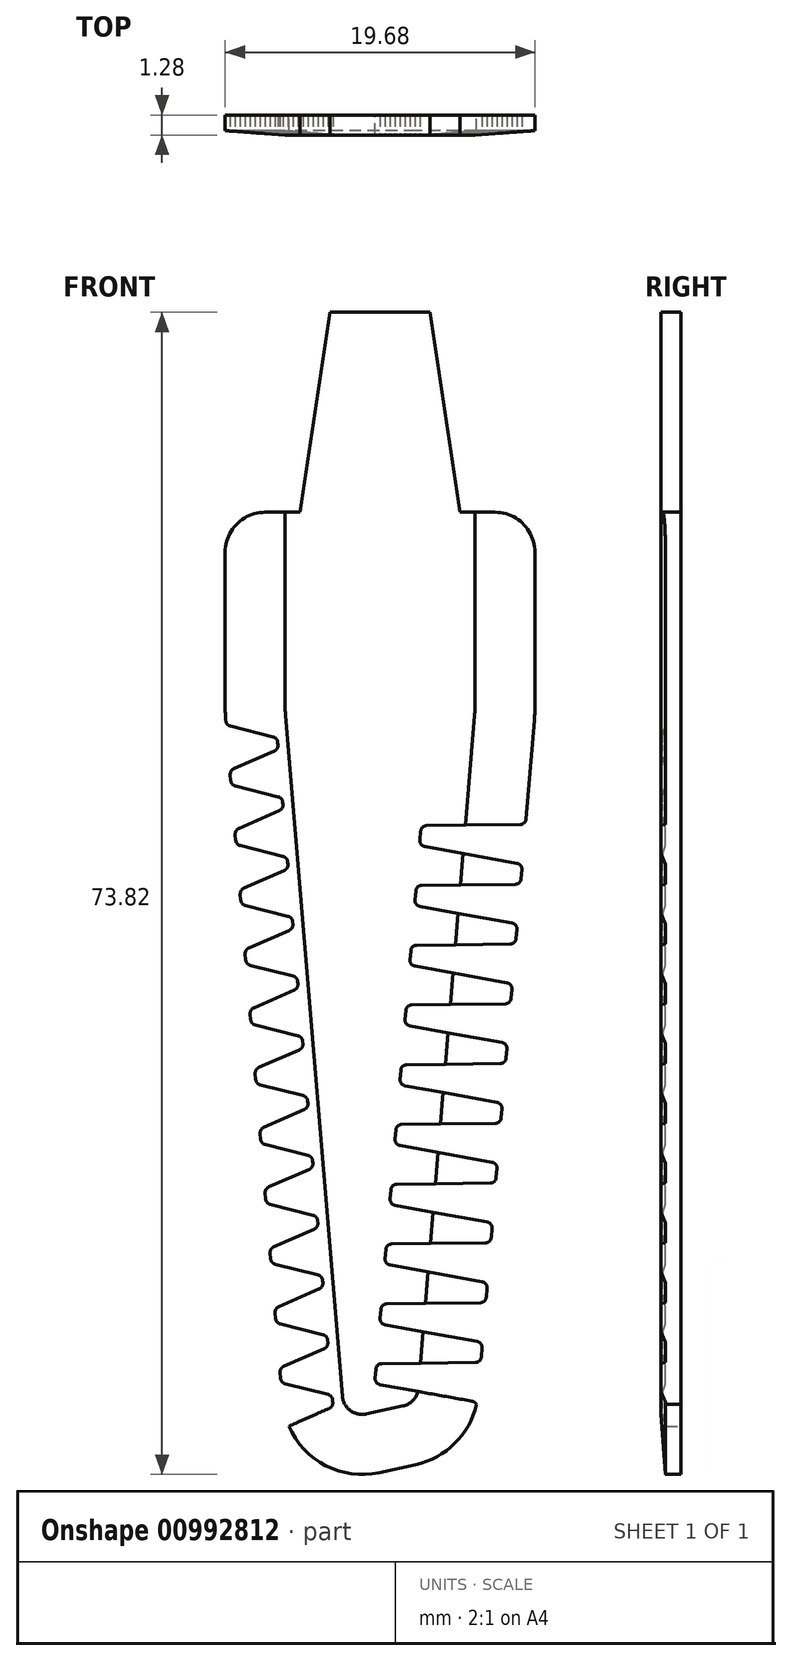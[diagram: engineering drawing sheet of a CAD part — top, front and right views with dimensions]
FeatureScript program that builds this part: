
annotation { "Feature Type Name" : "Feature", "Feature Type Description" : "" }
export const myFeature = defineFeature(function(context is Context, id is Id, definition is map)
    precondition{}
    {
        {
            var Q0;
            Q0=qCreatedBy(makeId("Front.planeOp"),FACE);
            var sketch = newSketch(context, id + "F0", { "sketchPlane" : qUnion([Q0])});
            skLineSegment(sketch, "E0", {"start": v(-5.71, -62.23) * mm, "end": v(0, -62.23) * mm});
            skLineSegment(sketch, "E1", {"start": v(0, -62.23) * mm, "end": v(5.72, -62.23) * mm});
            skLineSegment(sketch, "E2", {"start": v(5.72, -62.23) * mm, "end": v(9.84, -12.7) * mm});
            skLineSegment(sketch, "E3", {"start": v(9.84, 0) * mm, "end": v(0, 0) * mm});
            skLineSegment(sketch, "E4", {"start": v(-3.18, 0) * mm, "end": v(-3.18, 12.7) * mm});
            skLineSegment(sketch, "E5", {"start": v(-3.18, 12.7) * mm, "end": v(0, 12.7) * mm});
            skLineSegment(sketch, "E6", {"start": v(0, 12.7) * mm, "end": v(3.18, 12.7) * mm});
            skLineSegment(sketch, "E7", {"start": v(3.18, 12.7) * mm, "end": v(3.18, 0) * mm});
            skLineSegment(sketch, "E8", {"start": v(9.84, -12.7) * mm, "end": v(9.84, 0) * mm});
            skLineSegment(sketch, "E9", {"start": v(0, 0) * mm, "end": v(-9.84, 0) * mm});
            skLineSegment(sketch, "E10", {"start": v(-9.84, 0) * mm, "end": v(-9.84, -12.7) * mm});
            skLineSegment(sketch, "E11", {"start": v(-9.84, -12.7) * mm, "end": v(-5.71, -62.23) * mm});
            skLineSegment(sketch, "E12", {"start": v(-9.84, -12.7) * mm, "end": v(9.84, -12.7) * mm, "construction": true});
            skLineSegment(sketch, "E13", {"start": v(-5.72, -62.23) * mm, "end": v(5.93, -59.7) * mm});
            skSolve(sketch);
        }
        {
            var Q0;
            {var subQ0=sQuery(id+"F0.wireOp",EDGE,"E8");Q0=makeQuery(id+"F0.imprint","IMPRINT",FACE,{"disambiguationData":[TD([[makeQuery(id+"F0.imprint","IMPRINT",EDGE,{"derivedFrom":subQ0}),1.0]])]});}
            extrude(context, id + "F1", {"entities" : qUnion([Q0]), "endBound" : BoundingType.SYMMETRIC, "depth" : 1.27 * mm, "offsetDistance" : 25.4 * mm});
        }
        {
            var Q0;
            Q0=makeQuery(id+"F1.opExtrude","SWEPT_EDGE",EDGE,{"disambiguationData":[OSD([sQuery(id+"F0.wireOp",EDGE,"E10"),sQuery(id+"F0.wireOp",EDGE,"E11")])]});
            var Q1;
            Q1=makeQuery(id+"F1.opExtrude","SWEPT_EDGE",EDGE,{"disambiguationData":[OSD([sQuery(id+"F0.wireOp",EDGE,"E2"),sQuery(id+"F0.wireOp",EDGE,"E8")])]});
            fillet(context, id + "F2", {"entities" : qUnion([Q0, Q1]), "radius" : 12.7 * mm, "tangentPropagation" : true, "defaultsChanged" : false, "vertexSettings" : [], "allowEdgeOverflow" : false});
        }
        {
            var Q0;
            Q0=makeQuery(id+"F1.opExtrude","SWEPT_EDGE",EDGE,{"disambiguationData":[OSD([sQuery(id+"F0.wireOp",EDGE,"E3"),sQuery(id+"F0.wireOp",EDGE,"E8")])]});
            var Q1;
            Q1=makeQuery(id+"F1.opExtrude","SWEPT_EDGE",EDGE,{"disambiguationData":[OSD([sQuery(id+"F0.wireOp",EDGE,"E9"),sQuery(id+"F0.wireOp",EDGE,"E10")])]});
            fillet(context, id + "F3", {"entities" : qUnion([Q0, Q1]), "radius" : 2.54 * mm, "tangentPropagation" : true, "allowEdgeOverflow" : false});
        }
        {
            var Q0;
            Q0=makeQuery(id+"F11.boolean.opBoolean","MERGE",EDGE,{"derivedFrom":[makeQuery(id+"F1.opExtrude","SWEPT_EDGE",EDGE,{"disambiguationData":[OSD([sQuery(id+"F0.wireOp",EDGE,"qJLN5KsG-3gIc-xckK-YI7e-Zwq7uVVBdTZE"),sQuery(id+"F0.wireOp",EDGE,"E0")])]})],"fromTools":[makeQuery(id+"F11.opExtrude","SWEPT_EDGE",EDGE,{"disambiguationData":[OSD([sQuery(id+"F10.wireOp",EDGE,"E32"),sQuery(id+"F10.wireOp",EDGE,"E34")])]})]});
            fillet(context, id + "F4", {"entities" : qUnion([Q0]), "radius" : 5.08 * mm, "tangentPropagation" : true, "defaultsChanged" : true, "vertexSettings" : [], "allowEdgeOverflow" : false});
        }
        {
            var Q0;
            Q0=makeQuery(id+"F11.boolean.opBoolean","COPY",EDGE,{"derivedFrom":makeQuery(id+"F11.opExtrude","SWEPT_EDGE",EDGE,{"disambiguationData":[OSD([sQuery(id+"F10.wireOp",EDGE,"E32"),sQuery(id+"F10.wireOp",EDGE,"E33")])]})});
            var Q1;
            Q1=makeQuery(id+"F1.opExtrude","SWEPT_EDGE",EDGE,{"disambiguationData":[OSD([sQuery(id+"F0.wireOp",EDGE,"E1"),sQuery(id+"F0.wireOp",EDGE,"E2")])]});
            fillet(context, id + "F5", {"entities" : qUnion([Q0, Q1]), "radius" : 5.08 * mm, "tangentPropagation" : true, "defaultsChanged" : true, "vertexSettings" : [], "allowEdgeOverflow" : false});
        }
        {
            var Q0;
            Q0=qCreatedBy(makeId("Top.planeOp"),FACE);
            var sketch = newSketch(context, id + "F6", { "sketchPlane" : qUnion([Q0])});
            skLineSegment(sketch, "E14", {"start": v(6.03, 0.63) * mm, "end": v(9.84, 0.64) * mm});
            skLineSegment(sketch, "E15", {"start": v(9.84, 0.64) * mm, "end": v(9.84, 0.35) * mm});
            skLineSegment(sketch, "E16", {"start": v(9.84, 0.35) * mm, "end": v(9.84, 0) * mm, "construction": true});
            skLineSegment(sketch, "E17", {"start": v(9.84, 0) * mm, "end": v(9.84, -0.35) * mm, "construction": true});
            skLineSegment(sketch, "E18", {"start": v(9.84, -0.35) * mm, "end": v(9.84, -0.64) * mm});
            skLineSegment(sketch, "E19", {"start": v(9.84, -0.64) * mm, "end": v(6.03, -0.64) * mm});
            skLineSegment(sketch, "E20", {"start": v(6.03, -0.64) * mm, "end": v(9.84, -0.35) * mm});
            skLineSegment(sketch, "E21", {"start": v(6.03, 0.63) * mm, "end": v(9.84, 0.35) * mm});
            skLineSegment(sketch, "E22", {"start": v(6.03, 0.63) * mm, "end": v(6.03, -0.64) * mm, "construction": true});
            skSolve(sketch);
        }
        {
            var Q0;
            Q0=qCreatedBy(makeId("Front.planeOp"),FACE);
            var sketch = newSketch(context, id + "F7", { "sketchPlane" : qUnion([Q0])});
            skArc(sketch, "E23.0", {"start": v(6.24, -55.95) * mm, "mid": v(5, -58.88) * mm, "end": v(2.25, -60.5) * mm});
            skArc(sketch, "E24.0", {"start": v(-0.05, -61) * mm, "mid": v(-4.15, -60.12) * mm, "end": v(-6.2, -56.46) * mm});
            skLineSegment(sketch, "E25", {"start": v(2.25, -60.5) * mm, "end": v(-0.05, -61) * mm});
            skLineSegment(sketch, "E26", {"start": v(-6.2, -56.46) * mm, "end": v(-9.8, -13.23) * mm});
            skArc(sketch, "E27.0", {"start": v(9.84, -12.17) * mm, "mid": v(9.83, -12.7) * mm, "end": v(9.8, -13.23) * mm});
            skLineSegment(sketch, "E28", {"start": v(9.84, -12.17) * mm, "end": v(9.84, 0) * mm});
            skLineSegment(sketch, "E29", {"start": v(9.8, -13.23) * mm, "end": v(6.24, -55.95) * mm});
            skArc(sketch, "E30.0", {"start": v(-9.8, -13.23) * mm, "mid": v(-9.83, -12.7) * mm, "end": v(-9.84, -12.17) * mm});
            skLineSegment(sketch, "E31", {"start": v(-9.84, -12.17) * mm, "end": v(-9.84, 1.67) * mm});
            skSolve(sketch);
        }
        {
            var Q0;
            Q0=makeQuery(id+"F6.imprint","IMPRINT",FACE,{"disambiguationData":[TD([[makeQuery(id+"F6.imprint","IMPRINT",EDGE,{"derivedFrom":sQuery(id+"F6.wireOp",EDGE,"E18")}),-1.0]])]});
            var Q1;
            Q1 = qConstructionFilter(qBodyType(qCreatedBy(id + "F6" ,EDGE), BodyType.WIRE), ConstructionObject.NO);
            var Q2;
            Q2 = qConstructionFilter(qBodyType(qCreatedBy(id + "F7" ,EDGE), BodyType.WIRE), ConstructionObject.NO);
            sweep(context, id + "F8", {"profiles" : qUnion([Q0]), "surfaceProfiles" : qUnion([Q1]), "path" : qUnion([Q2])});
        }
        {
            var Q0;
            Q0=makeQuery(id+"F8.opSweep","SWEPT_BODY",BODY,{"disambiguationData":[OSD([sQuery(id+"F6.wireOp",EDGE,"E14"),sQuery(id+"F6.wireOp",EDGE,"E15"),sQuery(id+"F6.wireOp",EDGE,"E21"),sQuery(id+"F7.wireOp",EDGE,"E28")])]});
            var Q1;
            Q1=makeQuery(id+"F8.opSweep","SWEPT_BODY",BODY,{"disambiguationData":[OSD([sQuery(id+"F6.wireOp",EDGE,"E18"),sQuery(id+"F6.wireOp",EDGE,"E19"),sQuery(id+"F6.wireOp",EDGE,"E20"),sQuery(id+"F7.wireOp",EDGE,"E28")])]});
            var Q2;
            Q2=makeQuery(id+"F1.opExtrude","SWEPT_BODY",BODY,{"disambiguationData":[OSD([sQuery(id+"F0.wireOp",EDGE,"E0"),sQuery(id+"F0.wireOp",EDGE,"E1"),sQuery(id+"F0.wireOp",EDGE,"E2"),sQuery(id+"F0.wireOp",EDGE,"E3"),sQuery(id+"F0.wireOp",EDGE,"E4"),sQuery(id+"F0.wireOp",EDGE,"E5"),sQuery(id+"F0.wireOp",EDGE,"E6"),sQuery(id+"F0.wireOp",EDGE,"E7"),sQuery(id+"F0.wireOp",EDGE,"E8"),sQuery(id+"F0.wireOp",EDGE,"E9"),sQuery(id+"F0.wireOp",EDGE,"E10"),sQuery(id+"F0.wireOp",EDGE,"E11")])]});
            booleanBodies(context, id + "F9", {"operationType" : BooleanOperationType.SUBTRACTION, "tools" : qUnion([Q0, Q1]), "targets" : qUnion([Q2])});
        }
        {
            var Q0;
            Q0=qCreatedBy(makeId("Front.planeOp"),FACE);
            var sketch = newSketch(context, id + "F10", { "sketchPlane" : qUnion([Q0])});
            skLineSegment(sketch, "E32", {"start": v(-5.71, -62.23) * mm, "end": v(5.82, -60.96) * mm});
            skLineSegment(sketch, "E33", {"start": v(5.82, -60.96) * mm, "end": v(5.72, -62.23) * mm});
            skLineSegment(sketch, "E34", {"start": v(5.72, -62.23) * mm, "end": v(-5.71, -62.23) * mm});
            skSolve(sketch);
        }
        {
            var Q0;
            Q0=qSketchRegion(id+"F10",true);
            extrude(context, id + "F11", {"entities" : qUnion([Q0]), "operationType" : NewBodyOperationType.REMOVE, "endBound" : BoundingType.SYMMETRIC, "depth" : 25.4 * mm, "offsetDistance" : 25.4 * mm});
        }
        {
            var Q0;
            Q0=qCreatedBy(makeId("Front.planeOp"),FACE);
            var sketch = newSketch(context, id + "F12", { "sketchPlane" : qUnion([Q0])});
            skArc(sketch, "E35", {"start": v(6.16, -56.88) * mm, "mid": v(6.08, -56.61) * mm, "end": v(5.85, -56.47) * mm});
            skArc(sketch, "E36", {"start": v(6.05, -54) * mm, "mid": v(6.3, -53.9) * mm, "end": v(6.43, -53.65) * mm});
            skLineSegment(sketch, "E37", {"start": v(0.11, -54.08) * mm, "end": v(0, -55.41) * mm, "construction": true});
            skLineSegment(sketch, "E38", {"start": v(6.43, -53.65) * mm, "end": v(6.16, -56.88) * mm});
            skArc(sketch, "E39", {"start": v(0.11, -54.08) * mm, "mid": v(-0.14, -54.18) * mm, "end": v(-0.26, -54.43) * mm});
            skArc(sketch, "E40", {"start": v(-0.31, -55) * mm, "mid": v(-0.23, -55.27) * mm, "end": v(0, -55.41) * mm});
            skLineSegment(sketch, "E41", {"start": v(5.85, -56.47) * mm, "end": v(6.19, -56.53) * mm, "construction": true});
            skLineSegment(sketch, "E42", {"start": v(6.05, -54) * mm, "end": v(6.4, -54) * mm, "construction": true});
            skLineSegment(sketch, "E43", {"start": v(0, -55.41) * mm, "end": v(5.85, -56.47) * mm});
            skLineSegment(sketch, "E44", {"start": v(6.05, -54) * mm, "end": v(0.11, -54.08) * mm});
            skLineSegment(sketch, "E45", {"start": v(-0.31, -55) * mm, "end": v(-0.34, -55.35) * mm, "construction": true});
            skLineSegment(sketch, "E46", {"start": v(-0.34, -55.35) * mm, "end": v(0, -55.41) * mm, "construction": true});
            skLineSegment(sketch, "E47", {"start": v(-0.26, -54.43) * mm, "end": v(-0.24, -54.08) * mm, "construction": true});
            skLineSegment(sketch, "E48", {"start": v(-0.24, -54.08) * mm, "end": v(0.11, -54.08) * mm, "construction": true});
            skLineSegment(sketch, "E49", {"start": v(-0.29, -54.72) * mm, "end": v(6.3, -55.26) * mm, "construction": true});
            skLineSegment(sketch, "E50", {"start": v(-0.26, -54.43) * mm, "end": v(-0.29, -54.72) * mm});
            skLineSegment(sketch, "E51", {"start": v(-0.29, -54.72) * mm, "end": v(-0.31, -55) * mm});
            skSolve(sketch);
        }
        {
            var Q0;
            Q0=qSketchRegion(id+"F12",true);
            extrude(context, id + "F13", {"entities" : qUnion([Q0]), "operationType" : NewBodyOperationType.REMOVE, "endBound" : BoundingType.SYMMETRIC, "depth" : 25.4 * mm, "offsetDistance" : 25.4 * mm});
        }
        {
            var Q0;
            Q0=qCreatedBy(makeId("Front.planeOp"),FACE);
            var sketch = newSketch(context, id + "F14", { "sketchPlane" : qUnion([Q0])});
            skArc(sketch, "E52.0", {"start": v(6.05, -54) * mm, "mid": v(6.3, -53.9) * mm, "end": v(6.43, -53.65) * mm});
            skLineSegment(sketch, "E53.0", {"start": v(6.05, -54) * mm, "end": v(0.11, -54.08) * mm});
            skLineSegment(sketch, "E54.0", {"start": v(6.43, -53.65) * mm, "end": v(6.16, -56.88) * mm});
            skArc(sketch, "E55.0", {"start": v(6.16, -56.88) * mm, "mid": v(6.08, -56.61) * mm, "end": v(5.85, -56.47) * mm});
            skLineSegment(sketch, "E56.0", {"start": v(0, -55.41) * mm, "end": v(5.85, -56.47) * mm});
            skArc(sketch, "E57.0", {"start": v(0.11, -54.08) * mm, "mid": v(-0.14, -54.18) * mm, "end": v(-0.26, -54.43) * mm});
            skArc(sketch, "E58.0", {"start": v(-0.31, -55) * mm, "mid": v(-0.23, -55.27) * mm, "end": v(0, -55.41) * mm});
            skLineSegment(sketch, "E59.0", {"start": v(-0.26, -54.43) * mm, "end": v(-0.29, -54.72) * mm});
            skLineSegment(sketch, "E60.0", {"start": v(-0.29, -54.72) * mm, "end": v(-0.31, -55) * mm});
            skLineSegment(sketch, "E61.1.0.0", {"start": v(6.75, -49.86) * mm, "end": v(6.48, -53.08) * mm});
            skLineSegment(sketch, "E61.1.0.1", {"start": v(6.37, -50.2) * mm, "end": v(0.43, -50.28) * mm});
            skLineSegment(sketch, "E61.1.0.2", {"start": v(0.32, -51.61) * mm, "end": v(6.17, -52.67) * mm});
            skArc(sketch, "E61.1.0.3", {"start": v(6.37, -50.2) * mm, "mid": v(6.63, -50.1) * mm, "end": v(6.75, -49.86) * mm});
            skArc(sketch, "E61.1.0.4", {"start": v(6.48, -53.08) * mm, "mid": v(6.4, -52.81) * mm, "end": v(6.17, -52.67) * mm});
            skLineSegment(sketch, "E61.1.0.5", {"start": v(0.03, -50.92) * mm, "end": v(0, -51.2) * mm});
            skArc(sketch, "E61.1.0.6", {"start": v(0, -51.2) * mm, "mid": v(0.08, -51.47) * mm, "end": v(0.32, -51.61) * mm});
            skArc(sketch, "E61.1.0.7", {"start": v(0.43, -50.28) * mm, "mid": v(0.17, -50.38) * mm, "end": v(0.05, -50.63) * mm});
            skLineSegment(sketch, "E61.1.0.8", {"start": v(0.05, -50.63) * mm, "end": v(0.03, -50.92) * mm});
            skLineSegment(sketch, "E61.2.0.0", {"start": v(7.06, -46.06) * mm, "end": v(6.8, -49.28) * mm});
            skLineSegment(sketch, "E61.2.0.1", {"start": v(6.69, -46.4) * mm, "end": v(0.74, -46.49) * mm});
            skLineSegment(sketch, "E61.2.0.2", {"start": v(0.63, -47.82) * mm, "end": v(6.48, -48.88) * mm});
            skArc(sketch, "E61.2.0.3", {"start": v(6.69, -46.4) * mm, "mid": v(6.94, -46.3) * mm, "end": v(7.06, -46.06) * mm});
            skArc(sketch, "E61.2.0.4", {"start": v(6.8, -49.28) * mm, "mid": v(6.72, -49.02) * mm, "end": v(6.48, -48.88) * mm});
            skLineSegment(sketch, "E61.2.0.5", {"start": v(0.34, -47.12) * mm, "end": v(0.32, -47.41) * mm});
            skArc(sketch, "E61.2.0.6", {"start": v(0.32, -47.41) * mm, "mid": v(0.4, -47.67) * mm, "end": v(0.63, -47.82) * mm});
            skArc(sketch, "E61.2.0.7", {"start": v(0.74, -46.49) * mm, "mid": v(0.49, -46.59) * mm, "end": v(0.37, -46.83) * mm});
            skLineSegment(sketch, "E61.2.0.8", {"start": v(0.37, -46.83) * mm, "end": v(0.34, -47.12) * mm});
            skLineSegment(sketch, "E61.3.0.0", {"start": v(7.38, -42.26) * mm, "end": v(7.11, -45.48) * mm});
            skLineSegment(sketch, "E61.3.0.1", {"start": v(7, -42.61) * mm, "end": v(1.06, -42.69) * mm});
            skLineSegment(sketch, "E61.3.0.2", {"start": v(0.95, -44.02) * mm, "end": v(6.8, -45.08) * mm});
            skArc(sketch, "E61.3.0.3", {"start": v(7, -42.61) * mm, "mid": v(7.26, -42.51) * mm, "end": v(7.38, -42.26) * mm});
            skArc(sketch, "E61.3.0.4", {"start": v(7.11, -45.48) * mm, "mid": v(7.03, -45.22) * mm, "end": v(6.8, -45.08) * mm});
            skLineSegment(sketch, "E61.3.0.5", {"start": v(0.66, -43.33) * mm, "end": v(0.64, -43.61) * mm});
            skArc(sketch, "E61.3.0.6", {"start": v(0.64, -43.61) * mm, "mid": v(0.71, -43.88) * mm, "end": v(0.95, -44.02) * mm});
            skArc(sketch, "E61.3.0.7", {"start": v(1.06, -42.69) * mm, "mid": v(0.8, -42.8) * mm, "end": v(0.69, -43.04) * mm});
            skLineSegment(sketch, "E61.3.0.8", {"start": v(0.69, -43.04) * mm, "end": v(0.66, -43.33) * mm});
            skLineSegment(sketch, "E61.4.0.0", {"start": v(7.7, -38.47) * mm, "end": v(7.43, -41.69) * mm});
            skLineSegment(sketch, "E61.4.0.1", {"start": v(7.32, -38.82) * mm, "end": v(1.38, -38.9) * mm});
            skLineSegment(sketch, "E61.4.0.2", {"start": v(1.27, -40.22) * mm, "end": v(7.11, -41.28) * mm});
            skArc(sketch, "E61.4.0.3", {"start": v(7.32, -38.82) * mm, "mid": v(7.58, -38.71) * mm, "end": v(7.7, -38.47) * mm});
            skArc(sketch, "E61.4.0.4", {"start": v(7.43, -41.69) * mm, "mid": v(7.35, -41.42) * mm, "end": v(7.11, -41.28) * mm});
            skLineSegment(sketch, "E61.4.0.5", {"start": v(0.98, -39.53) * mm, "end": v(0.95, -39.82) * mm});
            skArc(sketch, "E61.4.0.6", {"start": v(0.95, -39.82) * mm, "mid": v(1.03, -40.08) * mm, "end": v(1.27, -40.22) * mm});
            skArc(sketch, "E61.4.0.7", {"start": v(1.38, -38.9) * mm, "mid": v(1.12, -39) * mm, "end": v(1, -39.24) * mm});
            skLineSegment(sketch, "E61.4.0.8", {"start": v(1, -39.24) * mm, "end": v(0.98, -39.53) * mm});
            skLineSegment(sketch, "E61.5.0.0", {"start": v(8.01, -34.67) * mm, "end": v(7.74, -37.9) * mm});
            skLineSegment(sketch, "E61.5.0.1", {"start": v(7.64, -35.02) * mm, "end": v(1.7, -35.1) * mm});
            skLineSegment(sketch, "E61.5.0.2", {"start": v(1.58, -36.43) * mm, "end": v(7.43, -37.48) * mm});
            skArc(sketch, "E61.5.0.3", {"start": v(7.64, -35.02) * mm, "mid": v(7.9, -34.92) * mm, "end": v(8.01, -34.67) * mm});
            skArc(sketch, "E61.5.0.4", {"start": v(7.74, -37.9) * mm, "mid": v(7.67, -37.63) * mm, "end": v(7.43, -37.48) * mm});
            skLineSegment(sketch, "E61.5.0.5", {"start": v(1.3, -35.73) * mm, "end": v(1.27, -36.02) * mm});
            skArc(sketch, "E61.5.0.6", {"start": v(1.27, -36.02) * mm, "mid": v(1.35, -36.28) * mm, "end": v(1.58, -36.43) * mm});
            skArc(sketch, "E61.5.0.7", {"start": v(1.7, -35.1) * mm, "mid": v(1.44, -35.2) * mm, "end": v(1.32, -35.44) * mm});
            skLineSegment(sketch, "E61.5.0.8", {"start": v(1.32, -35.44) * mm, "end": v(1.3, -35.73) * mm});
            skLineSegment(sketch, "E61.6.0.0", {"start": v(8.33, -30.87) * mm, "end": v(8.06, -34.1) * mm});
            skLineSegment(sketch, "E61.6.0.1", {"start": v(7.95, -31.22) * mm, "end": v(2, -31.3) * mm});
            skLineSegment(sketch, "E61.6.0.2", {"start": v(1.9, -32.63) * mm, "end": v(7.75, -33.69) * mm});
            skArc(sketch, "E61.6.0.3", {"start": v(7.95, -31.22) * mm, "mid": v(8.2, -31.12) * mm, "end": v(8.33, -30.87) * mm});
            skArc(sketch, "E61.6.0.4", {"start": v(8.06, -34.1) * mm, "mid": v(7.98, -33.83) * mm, "end": v(7.75, -33.69) * mm});
            skLineSegment(sketch, "E61.6.0.5", {"start": v(1.61, -31.94) * mm, "end": v(1.59, -32.22) * mm});
            skArc(sketch, "E61.6.0.6", {"start": v(1.59, -32.22) * mm, "mid": v(1.66, -32.49) * mm, "end": v(1.9, -32.63) * mm});
            skArc(sketch, "E61.6.0.7", {"start": v(2, -31.3) * mm, "mid": v(1.75, -31.4) * mm, "end": v(1.63, -31.65) * mm});
            skLineSegment(sketch, "E61.6.0.8", {"start": v(1.63, -31.65) * mm, "end": v(1.61, -31.94) * mm});
            skLineSegment(sketch, "E61.7.0.0", {"start": v(8.64, -27.08) * mm, "end": v(8.38, -30.3) * mm});
            skLineSegment(sketch, "E61.7.0.1", {"start": v(8.27, -27.43) * mm, "end": v(2.33, -27.5) * mm});
            skLineSegment(sketch, "E61.7.0.2", {"start": v(2.21, -28.83) * mm, "end": v(8.06, -29.9) * mm});
            skArc(sketch, "E61.7.0.3", {"start": v(8.27, -27.43) * mm, "mid": v(8.52, -27.32) * mm, "end": v(8.64, -27.08) * mm});
            skArc(sketch, "E61.7.0.4", {"start": v(8.38, -30.3) * mm, "mid": v(8.3, -30.03) * mm, "end": v(8.06, -29.9) * mm});
            skLineSegment(sketch, "E61.7.0.5", {"start": v(1.93, -28.14) * mm, "end": v(1.9, -28.43) * mm});
            skArc(sketch, "E61.7.0.6", {"start": v(1.9, -28.43) * mm, "mid": v(1.98, -28.69) * mm, "end": v(2.21, -28.83) * mm});
            skArc(sketch, "E61.7.0.7", {"start": v(2.33, -27.5) * mm, "mid": v(2.07, -27.6) * mm, "end": v(1.95, -27.85) * mm});
            skLineSegment(sketch, "E61.7.0.8", {"start": v(1.95, -27.85) * mm, "end": v(1.93, -28.14) * mm});
            skLineSegment(sketch, "E61.8.0.0", {"start": v(8.96, -23.28) * mm, "end": v(8.7, -26.5) * mm});
            skLineSegment(sketch, "E61.8.0.1", {"start": v(8.59, -23.63) * mm, "end": v(2.64, -23.7) * mm});
            skLineSegment(sketch, "E61.8.0.2", {"start": v(2.53, -25.04) * mm, "end": v(8.38, -26.1) * mm});
            skArc(sketch, "E61.8.0.3", {"start": v(8.59, -23.63) * mm, "mid": v(8.84, -23.53) * mm, "end": v(8.96, -23.28) * mm});
            skArc(sketch, "E61.8.0.4", {"start": v(8.7, -26.5) * mm, "mid": v(8.62, -26.24) * mm, "end": v(8.38, -26.1) * mm});
            skLineSegment(sketch, "E61.8.0.5", {"start": v(2.24, -24.34) * mm, "end": v(2.22, -24.63) * mm});
            skArc(sketch, "E61.8.0.6", {"start": v(2.22, -24.63) * mm, "mid": v(2.3, -24.9) * mm, "end": v(2.53, -25.04) * mm});
            skArc(sketch, "E61.8.0.7", {"start": v(2.64, -23.7) * mm, "mid": v(2.39, -23.8) * mm, "end": v(2.27, -24.05) * mm});
            skLineSegment(sketch, "E61.8.0.8", {"start": v(2.27, -24.05) * mm, "end": v(2.24, -24.34) * mm});
            skLineSegment(sketch, "E61.9.0.0", {"start": v(9.28, -19.48) * mm, "end": v(9, -22.7) * mm});
            skLineSegment(sketch, "E61.9.0.1", {"start": v(8.9, -19.83) * mm, "end": v(2.96, -19.9) * mm});
            skLineSegment(sketch, "E61.9.0.2", {"start": v(2.85, -21.24) * mm, "end": v(8.7, -22.3) * mm});
            skArc(sketch, "E61.9.0.3", {"start": v(8.9, -19.83) * mm, "mid": v(9.16, -19.73) * mm, "end": v(9.28, -19.48) * mm});
            skArc(sketch, "E61.9.0.4", {"start": v(9, -22.7) * mm, "mid": v(8.93, -22.44) * mm, "end": v(8.7, -22.3) * mm});
            skLineSegment(sketch, "E61.9.0.5", {"start": v(2.56, -20.54) * mm, "end": v(2.54, -20.83) * mm});
            skArc(sketch, "E61.9.0.6", {"start": v(2.54, -20.83) * mm, "mid": v(2.61, -21.1) * mm, "end": v(2.85, -21.24) * mm});
            skArc(sketch, "E61.9.0.7", {"start": v(2.96, -19.9) * mm, "mid": v(2.7, -20) * mm, "end": v(2.58, -20.26) * mm});
            skLineSegment(sketch, "E61.9.0.8", {"start": v(2.58, -20.26) * mm, "end": v(2.56, -20.54) * mm});
            skLineSegment(sketch, "E61.direction1", {"start": v(0, -55.41) * mm, "end": v(0.32, -51.61) * mm, "construction": true});
            skSolve(sketch);
        }
        {
            var Q0;
            Q0=qSketchRegion(id+"F14",true);
            extrude(context, id + "F15", {"entities" : qUnion([Q0]), "operationType" : NewBodyOperationType.REMOVE, "endBound" : BoundingType.SYMMETRIC, "oppositeDirection" : true, "depth" : 25.4 * mm, "offsetDistance" : 25.4 * mm});
        }
        {
            var Q0;
            Q0=qCreatedBy(makeId("Front.planeOp"),FACE);
            var sketch = newSketch(context, id + "F16", { "sketchPlane" : qUnion([Q0])});
            skLineSegment(sketch, "E62", {"start": v(-5.08, 0) * mm, "end": v(-3.18, 12.7) * mm});
            skLineSegment(sketch, "E63", {"start": v(-3.18, 12.7) * mm, "end": v(3.18, 12.7) * mm});
            skLineSegment(sketch, "E64", {"start": v(3.18, 12.7) * mm, "end": v(5.08, 0) * mm});
            skLineSegment(sketch, "E65", {"start": v(5.08, 0) * mm, "end": v(0, 0) * mm});
            skLineSegment(sketch, "E66", {"start": v(0, 0) * mm, "end": v(-5.08, 0) * mm});
            skSolve(sketch);
        }
        {
            var Q0;
            Q0=qSketchRegion(id+"F16",true);
            extrude(context, id + "F17", {"entities" : qUnion([Q0]), "operationType" : NewBodyOperationType.ADD, "endBound" : BoundingType.SYMMETRIC, "depth" : 1.27 * mm, "offsetDistance" : 25.4 * mm});
        }
        {
            var Q0;
            Q0=qCreatedBy(makeId("Front.planeOp"),FACE);
            var sketch = newSketch(context, id + "F18", { "sketchPlane" : qUnion([Q0])});
            skLineSegment(sketch, "E67", {"start": v(-6.03, -58.43) * mm, "end": v(-6.32, -55.02) * mm});
            skArc(sketch, "E68", {"start": v(-5.8, -58.05) * mm, "mid": v(-5.98, -58.2) * mm, "end": v(-6.03, -58.43) * mm});
            skArc(sketch, "E69", {"start": v(-6.32, -55.02) * mm, "mid": v(-6.23, -55.23) * mm, "end": v(-6.03, -55.35) * mm});
            skLineSegment(sketch, "E70", {"start": v(-6.03, -55.35) * mm, "end": v(-3.3, -56.04) * mm});
            skLineSegment(sketch, "E71", {"start": v(-3.3, -56.04) * mm, "end": v(-3.23, -56.93) * mm, "construction": true});
            skLineSegment(sketch, "E72", {"start": v(-3.23, -56.93) * mm, "end": v(-5.8, -58.05) * mm});
            skArc(sketch, "E73", {"start": v(-3.02, -56.38) * mm, "mid": v(-3.1, -56.16) * mm, "end": v(-3.3, -56.04) * mm});
            skArc(sketch, "E74", {"start": v(-3.23, -56.93) * mm, "mid": v(-3.06, -56.77) * mm, "end": v(-3, -56.54) * mm});
            skLineSegment(sketch, "E75", {"start": v(-3.02, -56.38) * mm, "end": v(-3, -56.54) * mm});
            skLineSegment(sketch, "E76", {"start": v(-6.17, -56.72) * mm, "end": v(-3.27, -56.48) * mm, "construction": true});
            skLineSegment(sketch, "E77", {"start": v(-6.03, -58.43) * mm, "end": v(-5.71, -62.23) * mm, "construction": true});
            skLineSegment(sketch, "E78", {"start": v(-0.05, -61) * mm, "end": v(-5.72, -62.23) * mm, "construction": true});
            skSolve(sketch);
        }
        {
            var Q0;
            Q0=qCreatedBy(makeId("Front.planeOp"),FACE);
            var sketch = newSketch(context, id + "F19", { "sketchPlane" : qUnion([Q0])});
            skLineSegment(sketch, "E79.0", {"start": v(-6.03, -58.43) * mm, "end": v(-6.32, -55.02) * mm});
            skArc(sketch, "E80.0", {"start": v(-6.32, -55.02) * mm, "mid": v(-6.23, -55.23) * mm, "end": v(-6.03, -55.35) * mm});
            skLineSegment(sketch, "E81.0", {"start": v(-6.03, -55.35) * mm, "end": v(-3.3, -56.04) * mm});
            skArc(sketch, "E82.0", {"start": v(-3.02, -56.38) * mm, "mid": v(-3.1, -56.16) * mm, "end": v(-3.3, -56.04) * mm});
            skLineSegment(sketch, "E83.0", {"start": v(-3.02, -56.38) * mm, "end": v(-3, -56.54) * mm});
            skArc(sketch, "E84.0", {"start": v(-3.23, -56.93) * mm, "mid": v(-3.06, -56.77) * mm, "end": v(-3, -56.54) * mm});
            skLineSegment(sketch, "E85.0", {"start": v(-3.23, -56.93) * mm, "end": v(-5.8, -58.05) * mm});
            skArc(sketch, "E86.0", {"start": v(-5.8, -58.05) * mm, "mid": v(-5.98, -58.2) * mm, "end": v(-6.03, -58.43) * mm});
            skLineSegment(sketch, "E87.1.0.0", {"start": v(-6.35, -54.64) * mm, "end": v(-6.63, -51.22) * mm});
            skLineSegment(sketch, "E87.1.0.1", {"start": v(-6.35, -51.56) * mm, "end": v(-3.62, -52.24) * mm});
            skLineSegment(sketch, "E87.1.0.2", {"start": v(-3.55, -53.13) * mm, "end": v(-6.12, -54.26) * mm});
            skArc(sketch, "E87.1.0.3", {"start": v(-6.63, -51.22) * mm, "mid": v(-6.54, -51.43) * mm, "end": v(-6.35, -51.56) * mm});
            skArc(sketch, "E87.1.0.4", {"start": v(-6.12, -54.26) * mm, "mid": v(-6.3, -54.4) * mm, "end": v(-6.35, -54.64) * mm});
            skLineSegment(sketch, "E87.1.0.5", {"start": v(-3.33, -52.58) * mm, "end": v(-3.32, -52.75) * mm});
            skArc(sketch, "E87.1.0.6", {"start": v(-3.33, -52.58) * mm, "mid": v(-3.42, -52.37) * mm, "end": v(-3.62, -52.24) * mm});
            skArc(sketch, "E87.1.0.7", {"start": v(-3.55, -53.13) * mm, "mid": v(-3.37, -52.97) * mm, "end": v(-3.32, -52.75) * mm});
            skLineSegment(sketch, "E87.2.0.0", {"start": v(-6.66, -50.84) * mm, "end": v(-6.95, -47.42) * mm});
            skLineSegment(sketch, "E87.2.0.1", {"start": v(-6.66, -47.76) * mm, "end": v(-3.94, -48.45) * mm});
            skLineSegment(sketch, "E87.2.0.2", {"start": v(-3.86, -49.33) * mm, "end": v(-6.44, -50.46) * mm});
            skArc(sketch, "E87.2.0.3", {"start": v(-6.95, -47.42) * mm, "mid": v(-6.86, -47.64) * mm, "end": v(-6.66, -47.76) * mm});
            skArc(sketch, "E87.2.0.4", {"start": v(-6.44, -50.46) * mm, "mid": v(-6.61, -50.61) * mm, "end": v(-6.66, -50.84) * mm});
            skLineSegment(sketch, "E87.2.0.5", {"start": v(-3.65, -48.78) * mm, "end": v(-3.64, -48.95) * mm});
            skArc(sketch, "E87.2.0.6", {"start": v(-3.65, -48.78) * mm, "mid": v(-3.74, -48.57) * mm, "end": v(-3.94, -48.45) * mm});
            skArc(sketch, "E87.2.0.7", {"start": v(-3.86, -49.33) * mm, "mid": v(-3.69, -49.18) * mm, "end": v(-3.64, -48.95) * mm});
            skLineSegment(sketch, "E87.direction1", {"start": v(-6.03, -58.43) * mm, "end": v(-6.35, -54.64) * mm, "construction": true});
            skLineSegment(sketch, "E88.0.3.0", {"start": v(-6.98, -47.04) * mm, "end": v(-7.27, -43.63) * mm});
            skLineSegment(sketch, "E88.3.3.0", {"start": v(-6.98, -43.96) * mm, "end": v(-4.25, -44.65) * mm});
            skLineSegment(sketch, "E88.6.3.0", {"start": v(-4.18, -45.53) * mm, "end": v(-6.75, -46.66) * mm});
            skArc(sketch, "E88.9.3.0", {"start": v(-7.27, -43.63) * mm, "mid": v(-7.18, -43.84) * mm, "end": v(-6.98, -43.96) * mm});
            skArc(sketch, "E88.13.3.0", {"start": v(-6.75, -46.66) * mm, "mid": v(-6.93, -46.82) * mm, "end": v(-6.98, -47.04) * mm});
            skLineSegment(sketch, "E88.17.3.0", {"start": v(-3.97, -44.99) * mm, "end": v(-3.95, -45.15) * mm});
            skArc(sketch, "E88.20.3.0", {"start": v(-3.97, -44.99) * mm, "mid": v(-4.06, -44.77) * mm, "end": v(-4.25, -44.65) * mm});
            skArc(sketch, "E88.24.3.0", {"start": v(-4.18, -45.53) * mm, "mid": v(-4, -45.38) * mm, "end": v(-3.95, -45.15) * mm});
            skLineSegment(sketch, "E88.0.4.0", {"start": v(-7.3, -43.25) * mm, "end": v(-7.58, -39.83) * mm});
            skLineSegment(sketch, "E88.3.4.0", {"start": v(-7.3, -40.17) * mm, "end": v(-4.57, -40.85) * mm});
            skLineSegment(sketch, "E88.6.4.0", {"start": v(-4.5, -41.74) * mm, "end": v(-7.07, -42.87) * mm});
            skArc(sketch, "E88.9.4.0", {"start": v(-7.58, -39.83) * mm, "mid": v(-7.5, -40.04) * mm, "end": v(-7.3, -40.17) * mm});
            skArc(sketch, "E88.13.4.0", {"start": v(-7.07, -42.87) * mm, "mid": v(-7.24, -43.02) * mm, "end": v(-7.3, -43.25) * mm});
            skLineSegment(sketch, "E88.17.4.0", {"start": v(-4.28, -41.19) * mm, "end": v(-4.27, -41.36) * mm});
            skArc(sketch, "E88.20.4.0", {"start": v(-4.28, -41.19) * mm, "mid": v(-4.37, -40.97) * mm, "end": v(-4.57, -40.85) * mm});
            skArc(sketch, "E88.24.4.0", {"start": v(-4.5, -41.74) * mm, "mid": v(-4.32, -41.58) * mm, "end": v(-4.27, -41.36) * mm});
            skLineSegment(sketch, "E88.0.5.0", {"start": v(-7.61, -39.45) * mm, "end": v(-7.9, -36.03) * mm});
            skLineSegment(sketch, "E88.3.5.0", {"start": v(-7.61, -36.37) * mm, "end": v(-4.89, -37.06) * mm});
            skLineSegment(sketch, "E88.6.5.0", {"start": v(-4.81, -37.94) * mm, "end": v(-7.39, -39.07) * mm});
            skArc(sketch, "E88.9.5.0", {"start": v(-7.9, -36.03) * mm, "mid": v(-7.8, -36.25) * mm, "end": v(-7.61, -36.37) * mm});
            skArc(sketch, "E88.13.5.0", {"start": v(-7.39, -39.07) * mm, "mid": v(-7.56, -39.22) * mm, "end": v(-7.61, -39.45) * mm});
            skLineSegment(sketch, "E88.17.5.0", {"start": v(-4.6, -37.4) * mm, "end": v(-4.58, -37.56) * mm});
            skArc(sketch, "E88.20.5.0", {"start": v(-4.6, -37.4) * mm, "mid": v(-4.69, -37.18) * mm, "end": v(-4.89, -37.06) * mm});
            skArc(sketch, "E88.24.5.0", {"start": v(-4.81, -37.94) * mm, "mid": v(-4.64, -37.79) * mm, "end": v(-4.58, -37.56) * mm});
            skLineSegment(sketch, "E88.0.6.0", {"start": v(-7.93, -35.65) * mm, "end": v(-8.21, -32.23) * mm});
            skLineSegment(sketch, "E88.3.6.0", {"start": v(-7.93, -32.57) * mm, "end": v(-5.2, -33.26) * mm});
            skLineSegment(sketch, "E88.6.6.0", {"start": v(-5.13, -34.14) * mm, "end": v(-7.7, -35.27) * mm});
            skArc(sketch, "E88.9.6.0", {"start": v(-8.21, -32.23) * mm, "mid": v(-8.13, -32.45) * mm, "end": v(-7.93, -32.57) * mm});
            skArc(sketch, "E88.13.6.0", {"start": v(-7.7, -35.27) * mm, "mid": v(-7.88, -35.43) * mm, "end": v(-7.93, -35.65) * mm});
            skLineSegment(sketch, "E88.17.6.0", {"start": v(-4.92, -33.6) * mm, "end": v(-4.9, -33.76) * mm});
            skArc(sketch, "E88.20.6.0", {"start": v(-4.92, -33.6) * mm, "mid": v(-5, -33.38) * mm, "end": v(-5.2, -33.26) * mm});
            skArc(sketch, "E88.24.6.0", {"start": v(-5.13, -34.14) * mm, "mid": v(-4.95, -34) * mm, "end": v(-4.9, -33.76) * mm});
            skLineSegment(sketch, "E88.0.7.0", {"start": v(-8.25, -31.86) * mm, "end": v(-8.53, -28.44) * mm});
            skLineSegment(sketch, "E88.3.7.0", {"start": v(-8.24, -28.78) * mm, "end": v(-5.52, -29.46) * mm});
            skLineSegment(sketch, "E88.6.7.0", {"start": v(-5.44, -30.35) * mm, "end": v(-8.02, -31.47) * mm});
            skArc(sketch, "E88.9.7.0", {"start": v(-8.53, -28.44) * mm, "mid": v(-8.44, -28.65) * mm, "end": v(-8.24, -28.78) * mm});
            skArc(sketch, "E88.13.7.0", {"start": v(-8.02, -31.47) * mm, "mid": v(-8.2, -31.63) * mm, "end": v(-8.25, -31.86) * mm});
            skLineSegment(sketch, "E88.17.7.0", {"start": v(-5.23, -29.8) * mm, "end": v(-5.22, -29.97) * mm});
            skArc(sketch, "E88.20.7.0", {"start": v(-5.23, -29.8) * mm, "mid": v(-5.32, -29.58) * mm, "end": v(-5.52, -29.46) * mm});
            skArc(sketch, "E88.24.7.0", {"start": v(-5.44, -30.35) * mm, "mid": v(-5.27, -30.2) * mm, "end": v(-5.22, -29.97) * mm});
            skLineSegment(sketch, "E88.0.8.0", {"start": v(-8.56, -28.06) * mm, "end": v(-8.85, -24.64) * mm});
            skLineSegment(sketch, "E88.3.8.0", {"start": v(-8.56, -24.98) * mm, "end": v(-5.83, -25.66) * mm});
            skLineSegment(sketch, "E88.6.8.0", {"start": v(-5.76, -26.55) * mm, "end": v(-8.34, -27.68) * mm});
            skArc(sketch, "E88.9.8.0", {"start": v(-8.85, -24.64) * mm, "mid": v(-8.76, -24.86) * mm, "end": v(-8.56, -24.98) * mm});
            skArc(sketch, "E88.13.8.0", {"start": v(-8.34, -27.68) * mm, "mid": v(-8.51, -27.83) * mm, "end": v(-8.56, -28.06) * mm});
            skLineSegment(sketch, "E88.17.8.0", {"start": v(-5.55, -26) * mm, "end": v(-5.53, -26.17) * mm});
            skArc(sketch, "E88.20.8.0", {"start": v(-5.55, -26) * mm, "mid": v(-5.64, -25.79) * mm, "end": v(-5.83, -25.66) * mm});
            skArc(sketch, "E88.24.8.0", {"start": v(-5.76, -26.55) * mm, "mid": v(-5.59, -26.4) * mm, "end": v(-5.53, -26.17) * mm});
            skLineSegment(sketch, "E89.0.9.0", {"start": v(-8.88, -24.26) * mm, "end": v(-9.16, -20.84) * mm});
            skLineSegment(sketch, "E89.3.9.0", {"start": v(-8.88, -21.18) * mm, "end": v(-6.15, -21.87) * mm});
            skLineSegment(sketch, "E89.6.9.0", {"start": v(-6.08, -22.75) * mm, "end": v(-8.65, -23.88) * mm});
            skArc(sketch, "E89.9.9.0", {"start": v(-9.16, -20.84) * mm, "mid": v(-9.07, -21.06) * mm, "end": v(-8.88, -21.18) * mm});
            skArc(sketch, "E89.13.9.0", {"start": v(-8.65, -23.88) * mm, "mid": v(-8.83, -24.03) * mm, "end": v(-8.88, -24.26) * mm});
            skLineSegment(sketch, "E89.17.9.0", {"start": v(-5.86, -22.2) * mm, "end": v(-5.85, -22.37) * mm});
            skArc(sketch, "E89.20.9.0", {"start": v(-5.86, -22.2) * mm, "mid": v(-5.95, -22) * mm, "end": v(-6.15, -21.87) * mm});
            skArc(sketch, "E89.24.9.0", {"start": v(-6.08, -22.75) * mm, "mid": v(-5.9, -22.6) * mm, "end": v(-5.85, -22.37) * mm});
            skLineSegment(sketch, "E89.0.10.0", {"start": v(-9.2, -20.46) * mm, "end": v(-9.48, -17.05) * mm});
            skLineSegment(sketch, "E89.3.10.0", {"start": v(-9.2, -17.39) * mm, "end": v(-6.47, -18.07) * mm});
            skLineSegment(sketch, "E89.6.10.0", {"start": v(-6.4, -18.96) * mm, "end": v(-8.97, -20.08) * mm});
            skArc(sketch, "E89.9.10.0", {"start": v(-9.48, -17.05) * mm, "mid": v(-9.4, -17.26) * mm, "end": v(-9.2, -17.39) * mm});
            skArc(sketch, "E89.13.10.0", {"start": v(-8.97, -20.08) * mm, "mid": v(-9.14, -20.24) * mm, "end": v(-9.2, -20.46) * mm});
            skLineSegment(sketch, "E89.17.10.0", {"start": v(-6.18, -18.4) * mm, "end": v(-6.17, -18.58) * mm});
            skArc(sketch, "E89.20.10.0", {"start": v(-6.18, -18.4) * mm, "mid": v(-6.27, -18.2) * mm, "end": v(-6.47, -18.07) * mm});
            skArc(sketch, "E89.24.10.0", {"start": v(-6.4, -18.96) * mm, "mid": v(-6.22, -18.8) * mm, "end": v(-6.17, -18.58) * mm});
            skLineSegment(sketch, "E89.0.11.0", {"start": v(-9.51, -16.67) * mm, "end": v(-9.8, -13.25) * mm});
            skLineSegment(sketch, "E89.3.11.0", {"start": v(-9.5, -13.59) * mm, "end": v(-6.78, -14.27) * mm});
            skLineSegment(sketch, "E89.6.11.0", {"start": v(-6.71, -15.16) * mm, "end": v(-9.28, -16.29) * mm});
            skArc(sketch, "E89.9.11.0", {"start": v(-9.8, -13.25) * mm, "mid": v(-9.7, -13.47) * mm, "end": v(-9.5, -13.59) * mm});
            skArc(sketch, "E89.13.11.0", {"start": v(-9.28, -16.29) * mm, "mid": v(-9.46, -16.44) * mm, "end": v(-9.51, -16.67) * mm});
            skLineSegment(sketch, "E89.17.11.0", {"start": v(-6.5, -14.61) * mm, "end": v(-6.48, -14.78) * mm});
            skArc(sketch, "E89.20.11.0", {"start": v(-6.5, -14.61) * mm, "mid": v(-6.59, -14.4) * mm, "end": v(-6.78, -14.27) * mm});
            skArc(sketch, "E89.24.11.0", {"start": v(-6.71, -15.16) * mm, "mid": v(-6.54, -15) * mm, "end": v(-6.48, -14.78) * mm});
            skSolve(sketch);
        }
        {
            var Q0;
            Q0=qSketchRegion(id+"F19",true);
            extrude(context, id + "F20", {"entities" : qUnion([Q0]), "operationType" : NewBodyOperationType.REMOVE, "endBound" : BoundingType.SYMMETRIC, "oppositeDirection" : true, "depth" : 25.4 * mm, "offsetDistance" : 25.4 * mm});
        }
    });
